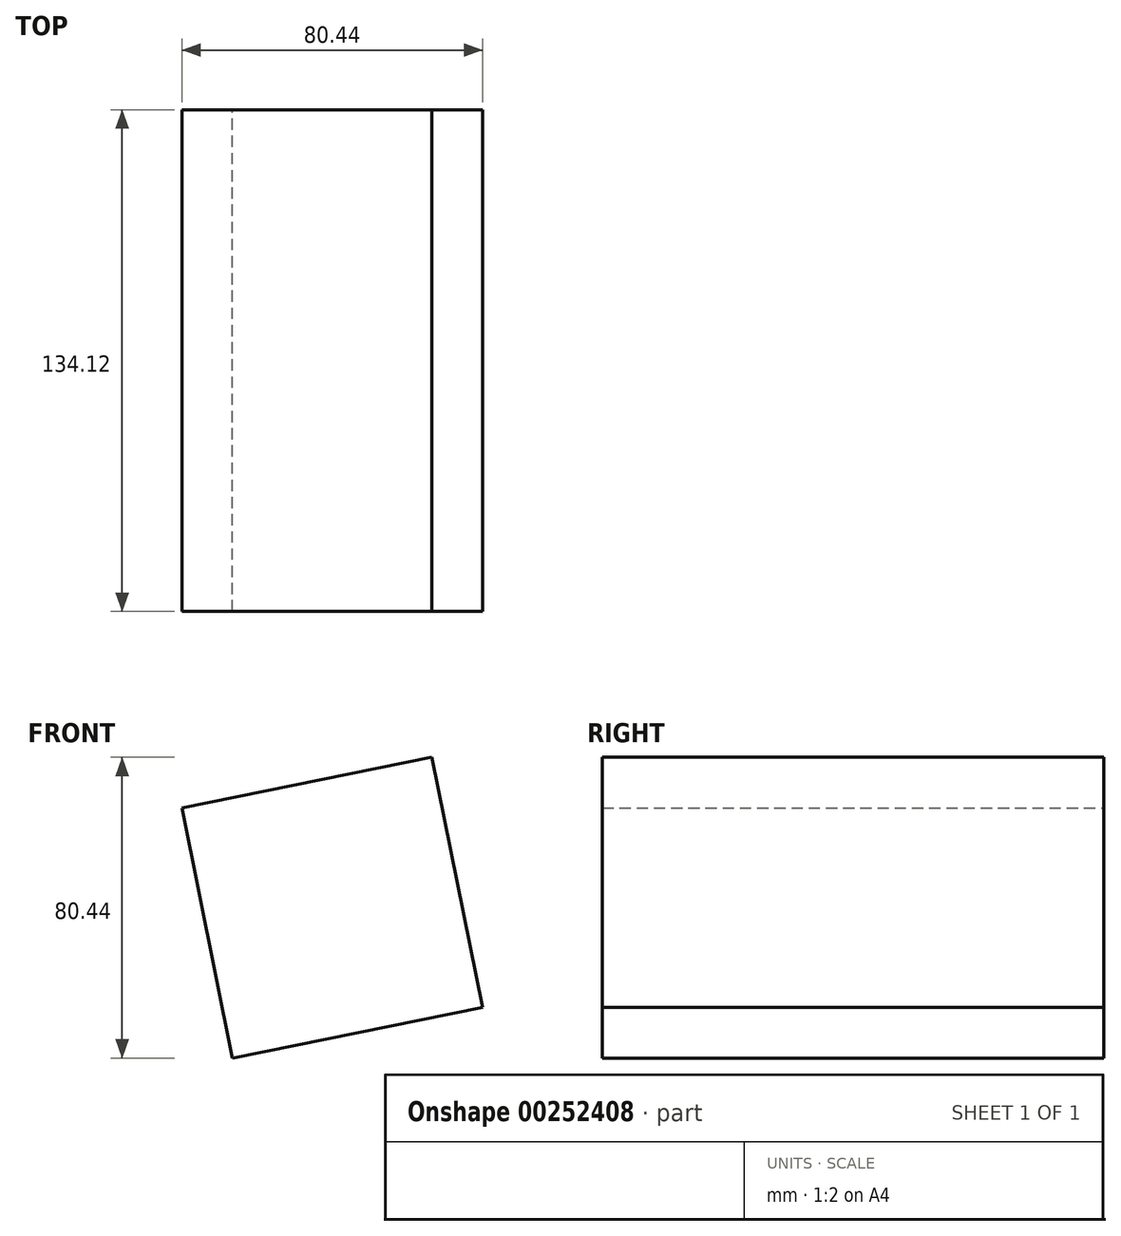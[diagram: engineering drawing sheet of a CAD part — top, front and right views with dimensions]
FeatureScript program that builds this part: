
annotation { "Feature Type Name" : "Feature", "Feature Type Description" : "" }
export const myFeature = defineFeature(function(context is Context, id is Id, definition is map)
    precondition{}
    {
        {
            var Q0;
            Q0=qCreatedBy(makeId("Front.planeOp"),FACE);
            var sketch = newSketch(context, id + "F0", { "sketchPlane" : qUnion([Q0])});
            skCircle(sketch, "E0.cCircle", {"center": v(0, 0) * mm, "radius": 48.26 * mm, "construction": true});
            skLineSegment(sketch, "E0.0", {"start": v(-40.22, 26.67) * mm, "end": v(26.67, 40.22) * mm});
            skLineSegment(sketch, "E0.1", {"start": v(26.67, 40.22) * mm, "end": v(40.22, -26.67) * mm});
            skLineSegment(sketch, "E0.2", {"start": v(40.22, -26.67) * mm, "end": v(-26.67, -40.22) * mm});
            skLineSegment(sketch, "E0.3", {"start": v(-26.67, -40.22) * mm, "end": v(-40.22, 26.67) * mm});
            skSolve(sketch);
        }
        {
            var Q0;
            Q0=makeQuery(id+"F0.imprint","IMPRINT",FACE,{"disambiguationData":[TD([[makeQuery(id+"F0.imprint","IMPRINT",EDGE,{"derivedFrom":sQuery(id+"F0.wireOp",EDGE,"E0.0")}),-1.0]])]});
            extrude(context, id + "F1", {"entities" : qUnion([Q0]), "endBound" : BoundingType.SYMMETRIC, "depth" : 134.11 * mm});
        }
    });
